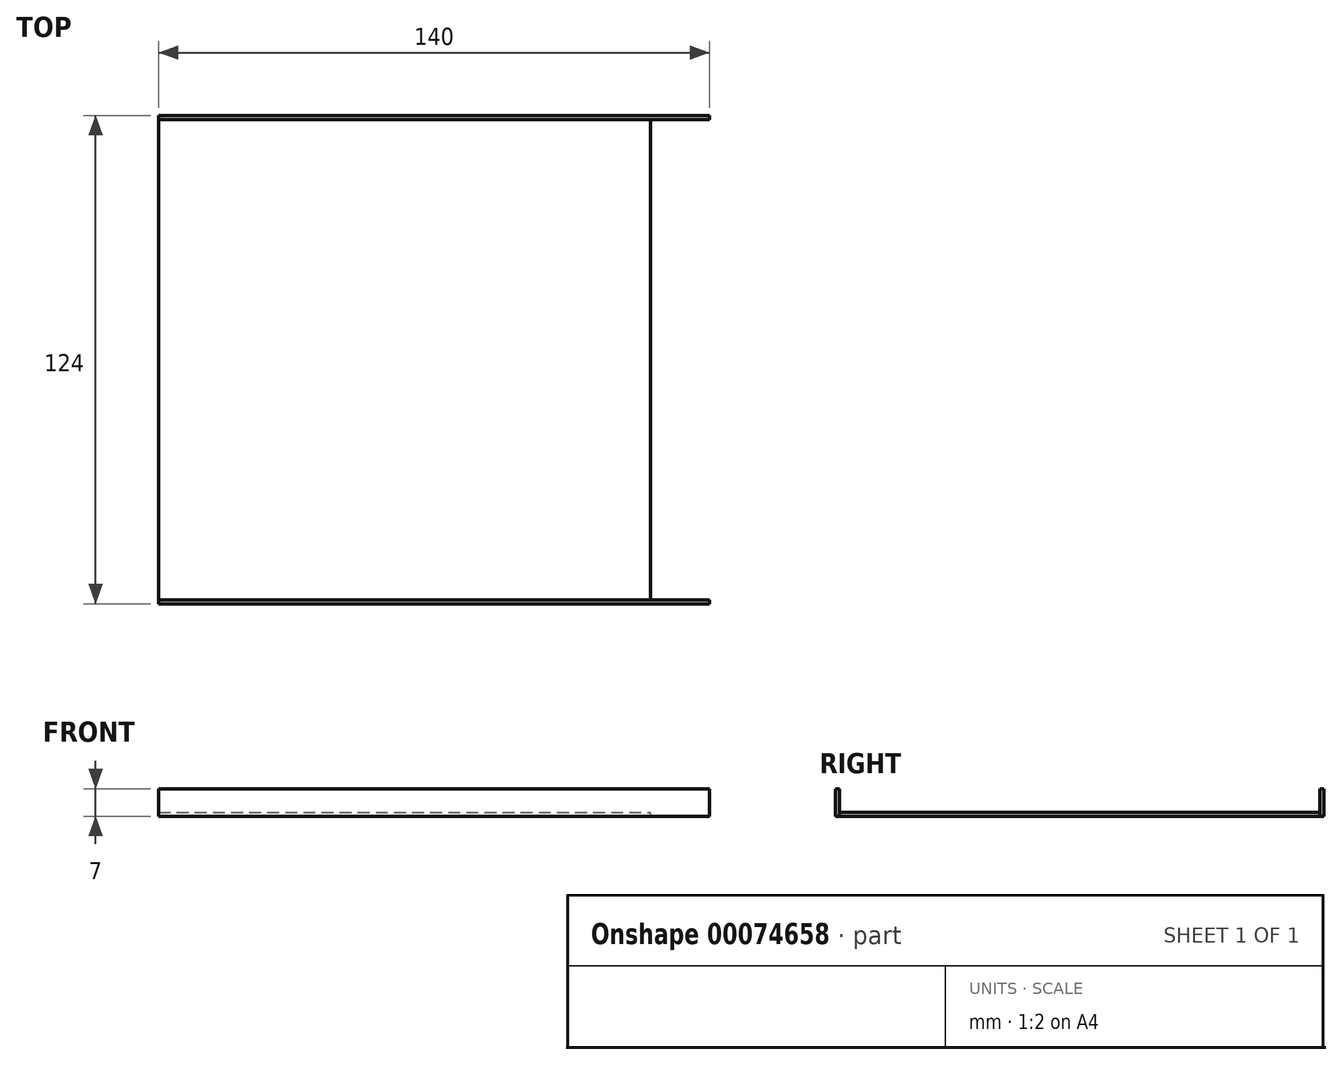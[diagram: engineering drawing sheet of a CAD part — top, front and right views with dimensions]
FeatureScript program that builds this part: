
annotation { "Feature Type Name" : "Feature", "Feature Type Description" : "" }
export const myFeature = defineFeature(function(context is Context, id is Id, definition is map)
    precondition{}
    {
        {
            var Q0;
            Q0=qCreatedBy(makeId("Top.planeOp"),FACE);
            var sketch = newSketch(context, id + "F0", { "sketchPlane" : qUnion([Q0])});
            skLineSegment(sketch, "E0.bottom", {"start": v(-88.47, 60.12) * mm, "end": v(51.53, 60.12) * mm});
            skLineSegment(sketch, "E0.top", {"start": v(-88.47, -63.88) * mm, "end": v(51.53, -63.88) * mm});
            skLineSegment(sketch, "E0.left", {"start": v(-88.47, 60.12) * mm, "end": v(-88.47, -63.88) * mm});
            skLineSegment(sketch, "E0.right", {"start": v(51.53, 60.12) * mm, "end": v(51.53, -63.88) * mm});
            skSolve(sketch);
        }
        {
            var Q0;
            Q0=makeQuery(id+"F0.imprint","IMPRINT",FACE,{"disambiguationData":[TD([[makeQuery(id+"F0.imprint","IMPRINT",EDGE,{"derivedFrom":sQuery(id+"F0.wireOp",EDGE,"E0.bottom")}),-1.0]])]});
            extrude(context, id + "F1", {"entities" : qUnion([Q0]), "depth" : 7 * mm});
        }
        {
            var Q0;
            Q0=makeQuery(id+"F1.opExtrude","CAP_FACE",FACE,{"disambiguationData":[OSD([sQuery(id+"F0.wireOp",EDGE,"E0.bottom"),sQuery(id+"F0.wireOp",EDGE,"E0.top"),sQuery(id+"F0.wireOp",EDGE,"E0.left"),sQuery(id+"F0.wireOp",EDGE,"E0.right")])],"isStart":false});
            shell(context, id + "F2", {"entities" : qUnion([Q0]), "thickness" : 1 * mm});
        }
        {
            var Q0;
            Q0=makeQuery(id+"F1.opExtrude","SWEPT_FACE",FACE,{"disambiguationData":[OSD([sQuery(id+"F0.wireOp",EDGE,"E0.left")])]});
            var sketch = newSketch(context, id + "F3", { "sketchPlane" : qUnion([Q0])});
            skLineSegment(sketch, "E1", {"start": v(-60.12, 7) * mm, "end": v(-60.12, 0) * mm});
            skLineSegment(sketch, "E2", {"start": v(-60.12, 0) * mm, "end": v(63.88, 0) * mm});
            skLineSegment(sketch, "E3", {"start": v(63.88, 0) * mm, "end": v(63.88, 7) * mm});
            skLineSegment(sketch, "E4.0", {"start": v(-59.12, 7) * mm, "end": v(-59.12, 0) * mm});
            skLineSegment(sketch, "E5.0", {"start": v(-60.12, 1) * mm, "end": v(63.88, 1) * mm});
            skLineSegment(sketch, "E6.0", {"start": v(62.88, 0) * mm, "end": v(62.88, 7) * mm});
            skSolve(sketch);
        }
        {
            var Q0;
            {var subQ0=sQuery(id+"F3.wireOp",EDGE,"E4.0");var subQ1=makeQuery(id+"F1.opExtrude","CAP_EDGE",EDGE,{"disambiguationData":[OSD([sQuery(id+"F0.wireOp",EDGE,"E0.left")])],"isStart":false});var subQ2=makeQuery(id+"F3.imprint","INTERSECT",VERTEX,{"derivedFrom":[subQ1,subQ0]});Q0=makeQuery(id+"F3.imprint","IMPRINT",FACE,{"disambiguationData":[TD([[makeQuery(id+"F3.imprint","IMPRINT",EDGE,{"disambiguationData":[TD([[subQ2,-1.0]])],"derivedFrom":subQ0}),1.0]])]});}
            extrude(context, id + "F4", {"entities" : qUnion([Q0]), "operationType" : NewBodyOperationType.REMOVE, "oppositeDirection" : true, "depth" : 1 * mm});
        }
        {
            var Q0;
            Q0=makeQuery(id+"F1.opExtrude","SWEPT_FACE",FACE,{"disambiguationData":[OSD([sQuery(id+"F0.wireOp",EDGE,"E0.right")])]});
            var sketch = newSketch(context, id + "F5", { "sketchPlane" : qUnion([Q0])});
            skLineSegment(sketch, "E7", {"start": v(60.12, 7) * mm, "end": v(60.12, 0) * mm});
            skLineSegment(sketch, "E8", {"start": v(60.12, 7) * mm, "end": v(-63.88, 7) * mm});
            skLineSegment(sketch, "E9", {"start": v(-63.88, 7) * mm, "end": v(-63.88, 0) * mm});
            skLineSegment(sketch, "E10.0", {"start": v(-62.88, 7) * mm, "end": v(-62.88, 0) * mm});
            skLineSegment(sketch, "E11.0", {"start": v(59.12, 7) * mm, "end": v(59.12, 0) * mm});
            skLineSegment(sketch, "E12", {"start": v(-63.88, 0) * mm, "end": v(59.12, 0) * mm});
            skLineSegment(sketch, "E13.0", {"start": v(-63.88, 1) * mm, "end": v(59.12, 1) * mm});
            skSolve(sketch);
        }
        {
            var Q0;
            {var subQ0=sQuery(id+"F5.wireOp",EDGE,"E10.0");var subQ1=sQuery(id+"F5.wireOp",EDGE,"E8");var subQ2=makeQuery(id+"F5.imprint","INTERSECT",VERTEX,{"derivedFrom":[subQ1,subQ0]});Q0=makeQuery(id+"F5.imprint","IMPRINT",FACE,{"disambiguationData":[TD([[makeQuery(id+"F5.imprint","IMPRINT",EDGE,{"disambiguationData":[TD([[subQ2,1.0]])],"derivedFrom":subQ1}),1.0]])]});}
            extrude(context, id + "F6", {"entities" : qUnion([Q0]), "operationType" : NewBodyOperationType.REMOVE, "oppositeDirection" : true, "depth" : 1 * mm});
        }
        {
            var Q0;
            Q0=makeQuery(id+"F6.boolean.opBoolean","MERGE",FACE,{"derivedFrom":[makeQuery(id+"F4.boolean.opBoolean","MERGE",FACE,{"derivedFrom":[makeQuery(id+"F2.opShell","OFFSET_FACE",FACE,{"disambiguationData":[OSD([sQuery(id+"F0.wireOp",EDGE,"E0.bottom"),sQuery(id+"F0.wireOp",EDGE,"E0.top"),sQuery(id+"F0.wireOp",EDGE,"E0.left"),sQuery(id+"F0.wireOp",EDGE,"E0.right")])]}),makeQuery(id+"F4.opExtrude","SWEPT_FACE",FACE,{"disambiguationData":[OSD([sQuery(id+"F3.wireOp",EDGE,"E5.0")])]})]}),makeQuery(id+"F6.opExtrude","SWEPT_FACE",FACE,{"disambiguationData":[OSD([sQuery(id+"F5.wireOp",EDGE,"E13.0")])]})]});
            var sketch = newSketch(context, id + "F7", { "sketchPlane" : qUnion([Q0])});
            skLineSegment(sketch, "E14.bottom", {"start": v(51.53, 59.12) * mm, "end": v(36.53, 59.12) * mm});
            skLineSegment(sketch, "E14.top", {"start": v(51.53, -62.88) * mm, "end": v(36.53, -62.88) * mm});
            skLineSegment(sketch, "E14.left", {"start": v(51.53, 59.12) * mm, "end": v(51.53, -62.88) * mm});
            skLineSegment(sketch, "E14.right", {"start": v(36.53, 59.12) * mm, "end": v(36.53, -62.88) * mm});
            skSolve(sketch);
        }
        {
            var Q0;
            Q0=makeQuery(id+"F7.imprint","IMPRINT",FACE,{"disambiguationData":[TD([[makeQuery(id+"F7.imprint","IMPRINT",EDGE,{"derivedFrom":sQuery(id+"F7.wireOp",EDGE,"E14.bottom")}),-1.0]])]});
            extrude(context, id + "F8", {"entities" : qUnion([Q0]), "operationType" : NewBodyOperationType.REMOVE, "oppositeDirection" : true, "depth" : 1 * mm});
        }
    });
